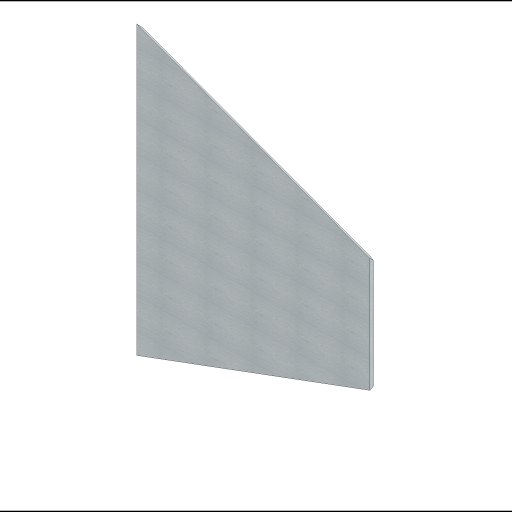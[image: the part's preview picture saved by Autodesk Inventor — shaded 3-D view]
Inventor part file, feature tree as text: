
AUTODESK INVENTOR PART (.ipt)
format: ipt  version: 2023 (Build 270158000, 158)  size: 266,240 bytes
history: native  units: in
note: dims shown in document units (in); Inventor stores cm internally (conversion verified against a paired STEP export)
features: sketch x8, extrude x4, loft x2, plane x2
ambient origin geometry x8: Origin, YZ Plane, XZ Plane, XY Plane, X Axis, Y Axis, Z Axis, Center Point
bodies: Solid1 (feature_tree)
feature tree (16):
  extrude  "Extrusion1"  Depth=33.0in
  loft  "Loft1"
  loft  "Loft2"
  plane  "Work Plane1"
  plane  "Work Plane2"
  extrude  "Extrusion3"  TaperAngle=135.0deg  [1 undecoded]
  extrude  "Extrusion4"  TaperAngle=0.0deg  [1 undecoded]
  extrude  "Extrusion6"  Depth=0.2947in
  sketch  "Sketch1"  dims[d0=27.0in d1=33.0in]
  sketch  "Sketch2"  dims[d2=4.0in d3=13.0in]
  sketch  "Sketch3"  dims[d4=10.0in d5=0.5in d6=0.0in]
  sketch  "Sketch4"  dims[d7=0.9422in d8=135.0deg]
  sketch  "Sketch5"  dims[d9=0.2947in d10=0.0in d11=90.0deg]
  sketch  "Sketch7"  dims[d12=0.0in d13=90.0deg d14=0.2947in]
  sketch  "Sketch8"  dims[d15=0.9422in]
  sketch  "Sketch10"  dims[d16=0.0in d17=90.0deg d18=0.0in d19=90.0deg d20=0.1554in d25=16.5in d26=0.469in d27=6.5in d28=0.0in d30=16.414in d31=0.0in d32=0.7661in d37=0.2295in d38=1.0in d39=1.0in d40=0.0in d41=0.0in]
note: 2 required parameter values undecoded (feature->parameter linkage not recoverable at this tier; creation-order binding heuristic only, values carry confidence <= 0.55)
